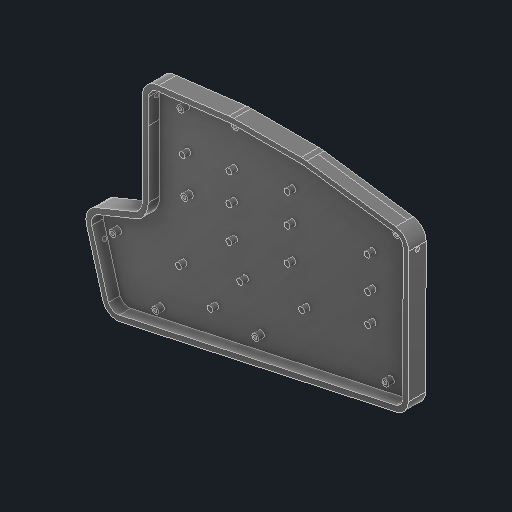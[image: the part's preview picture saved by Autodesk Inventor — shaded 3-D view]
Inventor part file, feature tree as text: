
AUTODESK INVENTOR PART (.ipt)
format: ipt  version: 2024.3 (Build 283343000, 343)  size: 350,720 bytes
history: native  units: in
note: dims shown in document units (in); Inventor stores cm internally (conversion verified against a paired STEP export)
features: sketch x6, other x3
ambient origin geometry x8: Origin, YZ Plane, XZ Plane, XY Plane, X Axis, Y Axis, Z Axis, Center Point
bodies: Solid1 (feature_tree)
feature tree (9):
  other  "Case Bottom.ipt"
  other  "Solid1::Case Bottom.ipt"
  other  "TaggingFeature1"
  sketch  "Sketch1"  dims[d0=0.3937in]
  sketch  "Sketch2"
  sketch  "Sketch3"
  sketch  "Sketch4"
  sketch  "Sketch5"
  sketch  "Sketch6"
